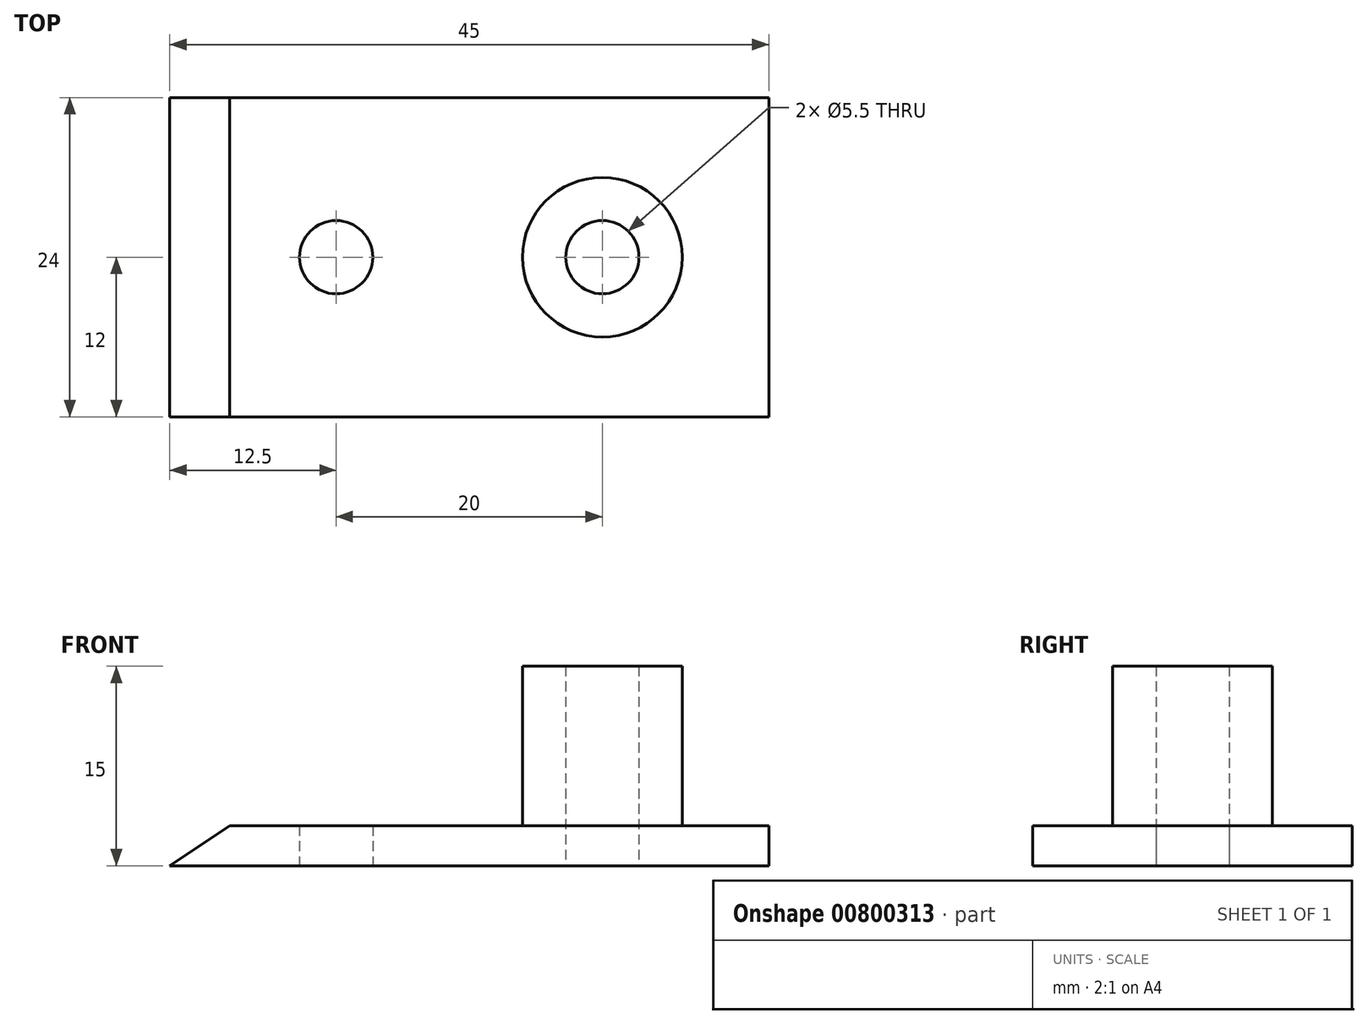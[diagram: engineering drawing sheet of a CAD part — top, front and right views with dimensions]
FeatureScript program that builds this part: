
annotation { "Feature Type Name" : "Feature", "Feature Type Description" : "" }
export const myFeature = defineFeature(function(context is Context, id is Id, definition is map)
    precondition{}
    {
        {
            var Q0;
            Q0=qCreatedBy(makeId("Top.planeOp"),FACE);
            var sketch = newSketch(context, id + "F0", { "sketchPlane" : qUnion([Q0])});
            skLineSegment(sketch, "E0.bottom", {"start": v(22.5, -12) * mm, "end": v(-22.5, -12) * mm});
            skLineSegment(sketch, "E0.top", {"start": v(22.5, 12) * mm, "end": v(-22.5, 12) * mm});
            skLineSegment(sketch, "E0.left", {"start": v(22.5, -12) * mm, "end": v(22.5, 12) * mm});
            skLineSegment(sketch, "E0.right", {"start": v(-22.5, -12) * mm, "end": v(-22.5, 12) * mm});
            skPoint(sketch, "E0.middle", {"position": v(0, 0) * mm});
            skLineSegment(sketch, "E1", {"start": v(0, 0) * mm, "end": v(-10, 0) * mm, "construction": true});
            skCircle(sketch, "E2", {"center": v(-10, 0) * mm, "radius": 2.75 * mm});
            skCircle(sketch, "E3.MirrorC", {"center": v(10, 0) * mm, "radius": 2.75 * mm});
            skSolve(sketch);
        }
        {
            var Q0;
            Q0 = qSketchRegion(id + "F0", true);
            extrude(context, id + "F1", {"entities" : qUnion([Q0]), "depth" : 15 * mm, "offsetDistance" : 25 * mm});
        }
        {
            var Q0;
            Q0=makeQuery(id+"F1.opExtrude","CAP_FACE",FACE,{"disambiguationData":[OSD([sQuery(id+"F0.wireOp",EDGE,"E0.bottom"),sQuery(id+"F0.wireOp",EDGE,"E0.top"),sQuery(id+"F0.wireOp",EDGE,"E0.left"),sQuery(id+"F0.wireOp",EDGE,"E0.right"),sQuery(id+"F0.wireOp",EDGE,"E2"),sQuery(id+"F0.wireOp",EDGE,"E3.MirrorC")])],"isStart":false});
            var sketch = newSketch(context, id + "F2", { "sketchPlane" : qUnion([Q0])});
            skCircle(sketch, "E4", {"center": v(-10, 0) * mm, "radius": 6 * mm});
            skCircle(sketch, "E5.MirrorC", {"center": v(10, 0) * mm, "radius": 6 * mm});
            skSolve(sketch);
        }
        {
            var Q0;
            Q0=makeQuery(id+"F2.imprint","IMPRINT",FACE,{"disambiguationData":[TD([[makeQuery(id+"F2.imprint","IMPRINT",EDGE,{"derivedFrom":sQuery(id+"F2.wireOp",EDGE,"E4")}),1.0]])]});
            var Q1;
            Q1=makeQuery(id+"F2.imprint","IMPRINT",FACE,{"disambiguationData":[TD([[makeQuery(id+"F2.imprint","IMPRINT",EDGE,{"derivedFrom":sQuery(id+"F2.wireOp",EDGE,"E5.MirrorC")}),-1.0]])]});
            extrude(context, id + "F3", {"entities" : qUnion([Q0, Q1]), "operationType" : NewBodyOperationType.REMOVE, "oppositeDirection" : true, "depth" : 12 * mm, "offsetDistance" : 25 * mm});
        }
        {
            var Q0;
            Q0=makeQuery(id+"F1.opExtrude","SWEPT_FACE",FACE,{"disambiguationData":[OSD([sQuery(id+"F0.wireOp",EDGE,"E0.bottom")])]});
            var sketch = newSketch(context, id + "F4", { "sketchPlane" : qUnion([Q0])});
            skLineSegment(sketch, "E6", {"start": v(0, 15) * mm, "end": v(0, 9) * mm, "construction": true});
            skCircle(sketch, "E7", {"center": v(0, 9) * mm, "radius": 2.75 * mm});
            skCircle(sketch, "E8", {"center": v(0, 9) * mm, "radius": 5 * mm});
            skLineSegment(sketch, "E9", {"start": v(-22.5, 0) * mm, "end": v(-2.77, 13.16) * mm});
            skLineSegment(sketch, "E10", {"start": v(22.5, 0) * mm, "end": v(2.77, 13.16) * mm});
            skSolve(sketch);
        }
        {
            var Q0;
            Q0=makeQuery(id+"F4.imprint","IMPRINT",FACE,{"disambiguationData":[TD([[makeQuery(id+"F4.imprint","IMPRINT",EDGE,{"derivedFrom":sQuery(id+"F4.wireOp",EDGE,"E7")}),1.0]])]});
            var Q1;
            {var subQ2=sQuery(id+"F4.wireOp",EDGE,"E9");Q1=makeQuery(id+"F4.imprint","IMPRINT",FACE,{"disambiguationData":[TD([[makeQuery(id+"F4.imprint","IMPRINT",EDGE,{"derivedFrom":subQ2}),1.0]])]});}
            extrude(context, id + "F5", {"entities" : qUnion([Q0, Q1]), "operationType" : NewBodyOperationType.REMOVE, "endBound" : BoundingType.THROUGH_ALL, "oppositeDirection" : true, "depth" : 25 * mm, "offsetDistance" : 25 * mm});
        }
    });
